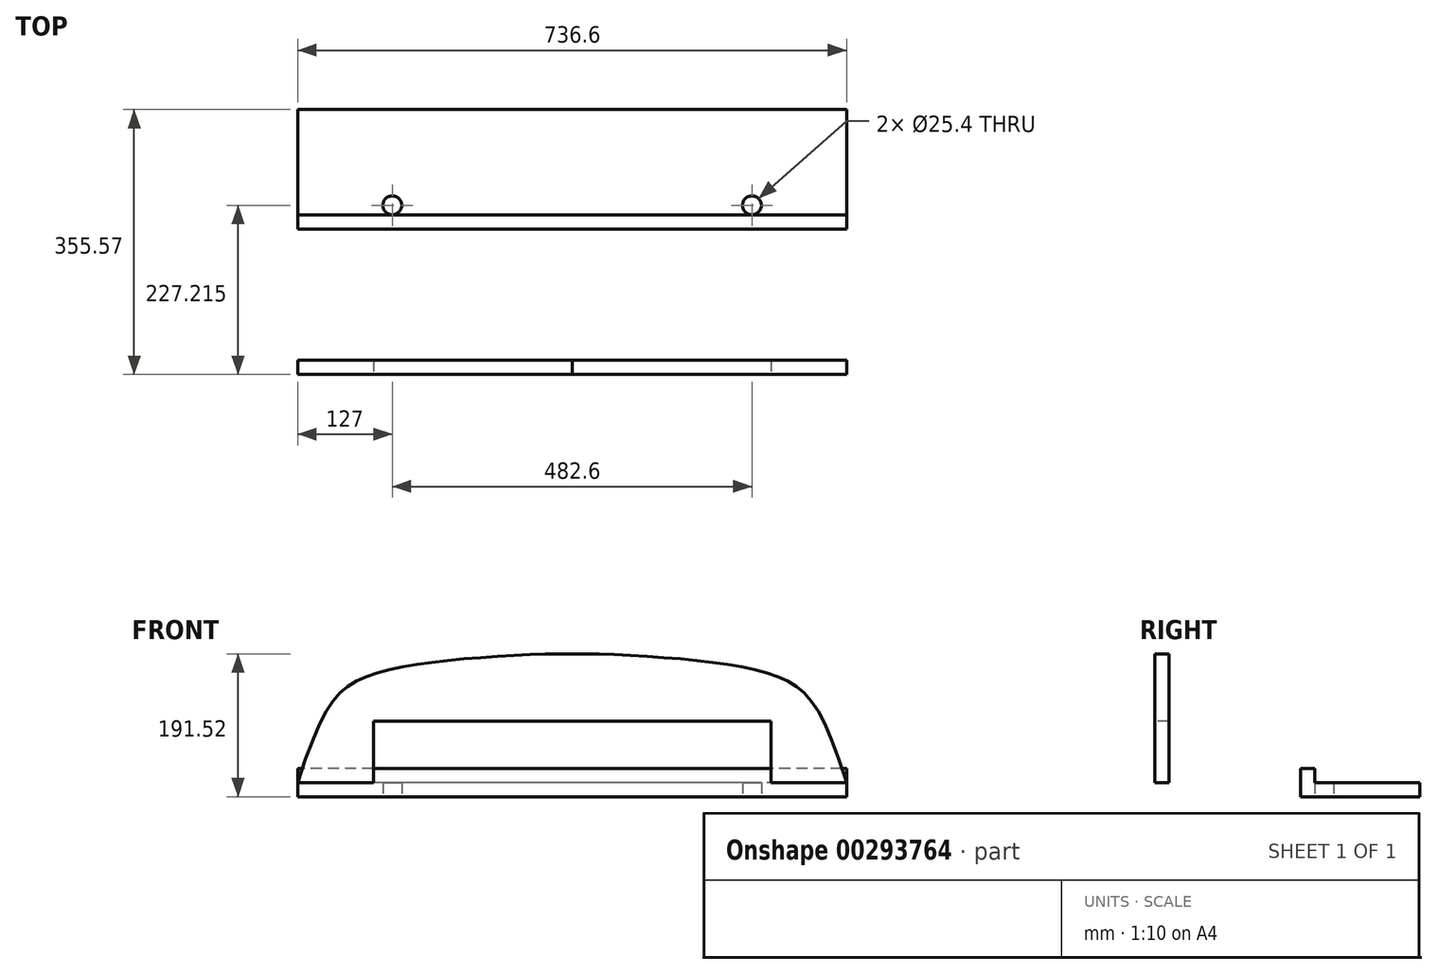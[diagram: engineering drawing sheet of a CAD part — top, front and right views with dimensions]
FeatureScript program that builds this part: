
annotation { "Feature Type Name" : "Feature", "Feature Type Description" : "" }
export const myFeature = defineFeature(function(context is Context, id is Id, definition is map)
    precondition{}
    {
        {
            var Q0;
            Q0=qCreatedBy(makeId("Top.planeOp"),FACE);
            var sketch = newSketch(context, id + "F0", { "sketchPlane" : qUnion([Q0])});
            skLineSegment(sketch, "E0.bottom", {"start": v(368.3, 214.52) * mm, "end": v(-368.3, 214.52) * mm});
            skLineSegment(sketch, "E0.top", {"start": v(368.3, 355.57) * mm, "end": v(-368.3, 355.57) * mm});
            skLineSegment(sketch, "E0.left", {"start": v(368.3, 214.52) * mm, "end": v(368.3, 355.57) * mm});
            skLineSegment(sketch, "E0.right", {"start": v(-368.3, 214.52) * mm, "end": v(-368.3, 355.57) * mm});
            skPoint(sketch, "E0.middle", {"position": v(0, 285.04) * mm});
            skSolve(sketch);
        }
        {
            var Q0;
            Q0=makeQuery(id+"F0.imprint","IMPRINT",FACE,{"disambiguationData":[TD([[makeQuery(id+"F0.imprint","IMPRINT",EDGE,{"derivedFrom":sQuery(id+"F0.wireOp",EDGE,"E0.bottom")}),-1.0]])]});
            extrude(context, id + "F1", {"entities" : qUnion([Q0]), "depth" : 19.05 * mm});
        }
        {
            var Q0;
            Q0=qCreatedBy(makeId("Top.planeOp"),FACE);
            var sketch = newSketch(context, id + "F2", { "sketchPlane" : qUnion([Q0])});
            skLineSegment(sketch, "E1.bottom", {"start": v(368.3, 214.52) * mm, "end": v(-368.3, 214.52) * mm});
            skLineSegment(sketch, "E1.top", {"start": v(368.3, 195.47) * mm, "end": v(-368.3, 195.47) * mm});
            skLineSegment(sketch, "E1.left", {"start": v(368.3, 214.52) * mm, "end": v(368.3, 195.47) * mm});
            skLineSegment(sketch, "E1.right", {"start": v(-368.3, 214.52) * mm, "end": v(-368.3, 195.47) * mm});
            skSolve(sketch);
        }
        {
            var Q0;
            Q0 = qSketchRegion(id + "F2", true);
            extrude(context, id + "F3", {"entities" : qUnion([Q0]), "operationType" : NewBodyOperationType.ADD, "depth" : 38.1 * mm});
        }
        {
            var Q0;
            Q0=qCreatedBy(makeId("Top.planeOp"),FACE);
            var sketch = newSketch(context, id + "F4", { "sketchPlane" : qUnion([Q0])});
            skCircle(sketch, "E2", {"center": v(241.3, 227.22) * mm, "radius": 12.7 * mm});
            skCircle(sketch, "E3.MirrorC", {"center": v(-241.3, 227.22) * mm, "radius": 12.7 * mm});
            skSolve(sketch);
        }
        {
            var Q0;
            Q0 = qSketchRegion(id + "F4", true);
            extrude(context, id + "F5", {"entities" : qUnion([Q0]), "operationType" : NewBodyOperationType.REMOVE, "depth" : 25.4 * mm});
        }
        {
            var Q0;
            Q0=qCreatedBy(makeId("Front.planeOp"),FACE);
            var sketch = newSketch(context, id + "F6", { "sketchPlane" : qUnion([Q0])});
            skFitSpline(sketch, "E4", {"points": [v(368.3, 19.05) * mm, v(291.75, 153.76) * mm, v(172.58, 182.18) * mm, v(0, 191.43) * mm], "startDerivative": vector(-257.91, 785.5) * mm, "endDerivative": vector(-369.28, -6.03) * mm});
            skLineSegment(sketch, "E5.bottom", {"start": v(0, 0) * mm, "end": v(266.7, 0) * mm});
            skLineSegment(sketch, "E5.top", {"start": v(0, 101.6) * mm, "end": v(266.7, 101.6) * mm});
            skLineSegment(sketch, "E5.left", {"start": v(0, 0) * mm, "end": v(0, 101.6) * mm});
            skLineSegment(sketch, "E5.right", {"start": v(266.7, 0) * mm, "end": v(266.7, 101.6) * mm});
            skLineSegment(sketch, "E6", {"start": v(368.3, 19.05) * mm, "end": v(266.7, 19.05) * mm});
            skFitSpline(sketch, "E7.MirrorCS", {"points": [v(-368.3, 19.05) * mm, v(-291.75, 153.76) * mm, v(-172.58, 182.18) * mm, v(0, 191.43) * mm], "startDerivative": vector(257.91, 785.5) * mm, "endDerivative": vector(369.28, -6.03) * mm});
            skLineSegment(sketch, "E8.MirrorCS", {"start": v(0, 101.6) * mm, "end": v(-266.7, 101.6) * mm});
            skLineSegment(sketch, "E9.MirrorCS", {"start": v(-266.7, 0) * mm, "end": v(-266.7, 101.6) * mm});
            skLineSegment(sketch, "E10.MirrorCS", {"start": v(-368.3, 19.05) * mm, "end": v(-266.7, 19.05) * mm});
            skSolve(sketch);
        }
        {
            var Q0;
            Q0=makeQuery(id+"F6.imprint","IMPRINT",FACE,{"disambiguationData":[TD([[makeQuery(id+"F6.imprint","IMPRINT",EDGE,{"derivedFrom":sQuery(id+"F6.wireOp",EDGE,"E4")}),1.0]])]});
            extrude(context, id + "F7", {"entities" : qUnion([Q0]), "oppositeDirection" : true, "depth" : 19.05 * mm});
        }
    });
